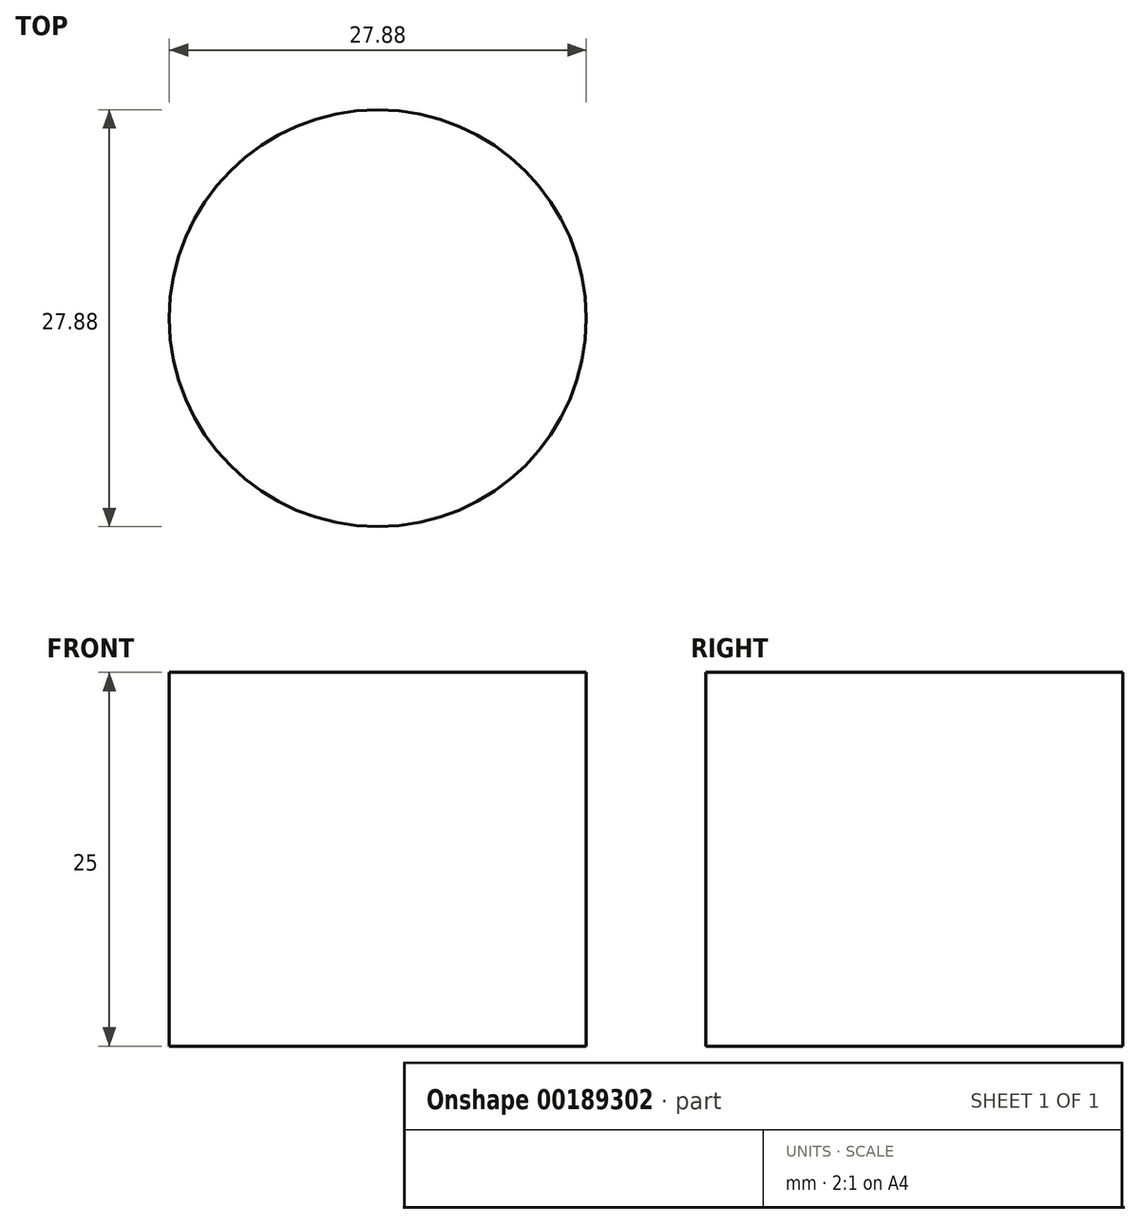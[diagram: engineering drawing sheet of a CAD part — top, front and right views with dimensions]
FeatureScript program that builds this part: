
annotation { "Feature Type Name" : "Feature", "Feature Type Description" : "" }
export const myFeature = defineFeature(function(context is Context, id is Id, definition is map)
    precondition{}
    {
        {
            var Q0;
            Q0=qCreatedBy(makeId("Top.planeOp"),FACE);
            var sketch = newSketch(context, id + "F0", { "sketchPlane" : qUnion([Q0])});
            skCircle(sketch, "E0", {"center": v(0, 0) * mm, "radius": 13.94 * mm});
            skSolve(sketch);
        }
        {
            var Q0;
            Q0=makeQuery(id+"F0.imprint","IMPRINT",FACE,{"disambiguationData":[TD([[makeQuery(id+"F0.imprint","IMPRINT",EDGE,{"derivedFrom":sQuery(id+"F0.wireOp",EDGE,"E0")}),1.0]])]});
            extrude(context, id + "F1", {"entities" : qUnion([Q0]), "depth" : 25 * mm});
        }
    });
